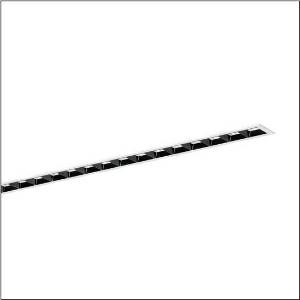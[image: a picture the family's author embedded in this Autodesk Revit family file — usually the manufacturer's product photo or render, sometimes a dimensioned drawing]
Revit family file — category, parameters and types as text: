
# Revit family: silica_r__21_51mx12db35wb_b505
name_source: partatom
category: Lighting Fixtures
units: mm (PartAtom-declared; Revit-internal decimal feet)

## family parameters
Cut with Voids When Loaded = No
Host = Face
Light Source = No
Part Type = Normal
Room Calculation Point = No
Round Connector Dimension = Use Diameter
Shared = No

## types (1)
- --- (1 x LED, 5400 lm, 34.3 W, 3000K)
    Apparent Load = 34 VA
    CIE Flux Codes = 86 100 100 100 100
    Color Rendering = 80
    Color Temperature = 3000K
    Default Elevation = 1800 mm
    Description = Silica® 21, office luminaire, primary light control with darklight reflector, of PMMA, black, CAT 2 (L<= 3000cd/m²), light emission: direct distribution, primary light characteristic: symmetric, installation type: recessed, LED, rated luminous flux: 5.400lm, luminous efficacy: 157lm/W, light colour: 830, colour temperature: 3000K, control gear: DALI 2, with terminal, 3+2-pole, max. 2.5mm², mains connection: 220..240V, AC, 50/60Hz, rated input power: 34.3W, luminaire housing, of aluminium, traffic white (RAL 9016), length: 1.528mm, width: 79mm, height: 53mm, protection rating (complete): IP20, insulation class (complete): insulation class I (protective earthing), certification: CE, ENEC, VDE, permissible operating ambient temperature: 0..+35°C, standard: EN 50419, packaging unit: 1 piece
    Height = 0 mm  [stored 0 ft]
    Lamp = 1 x LED
    Lamp Light Flux = 5400 lm
    Lamp Power = 34.3 W
    Lamp count = 1
    Length = 1527 mm
    Luminous efficacy = 157 lm/W
    Manufacturer = Siteco
    ModVariant = No
    Model = 51MX12DB35WB
    Mounting Place = Ceiling
    Mounting Type = Recessed
    Number of Poles = 1
    OnlyDefault = Yes
    Power Factor = 1
    Product Name = Silica® 21
    Product group = office luminaire | ceiling recessed
    ProductGroupID = 401
    Protection Class = Protection class I
    Protection Degree = IP 20
    RLX_Detail_Level = 1
    RLX_Emergency_Light_Flux = 0 lm
    RLX_Emergency_Type = 0
    RLX_Emergency_Type_DB = No
    RlxData = <blob elided: 42173 chars, md5=7188ceb7>
    Socket = socket
    Standby Power = 0 W
    System Light Flux = 5400 lm
    System Power = 34 W
    Type Comments = factory setting: luminous flux: 100 % | dim-lin: 254 | 392 mA
    Type Image = l_1335880.jpg
    URL = http://relux.com
    VarID = @adj_124420
    Voltage = 0 V
    Weight = 0.00 kg
    Width = 79 mm

note: [stored X ft] marks values corroborated as IEEE doubles in the binary element streams (Revit-internal decimal feet)

## geometry (parser evidence)
native form markers: Blend x4, Sweep x10
no freeform markers — native parametric forms only
